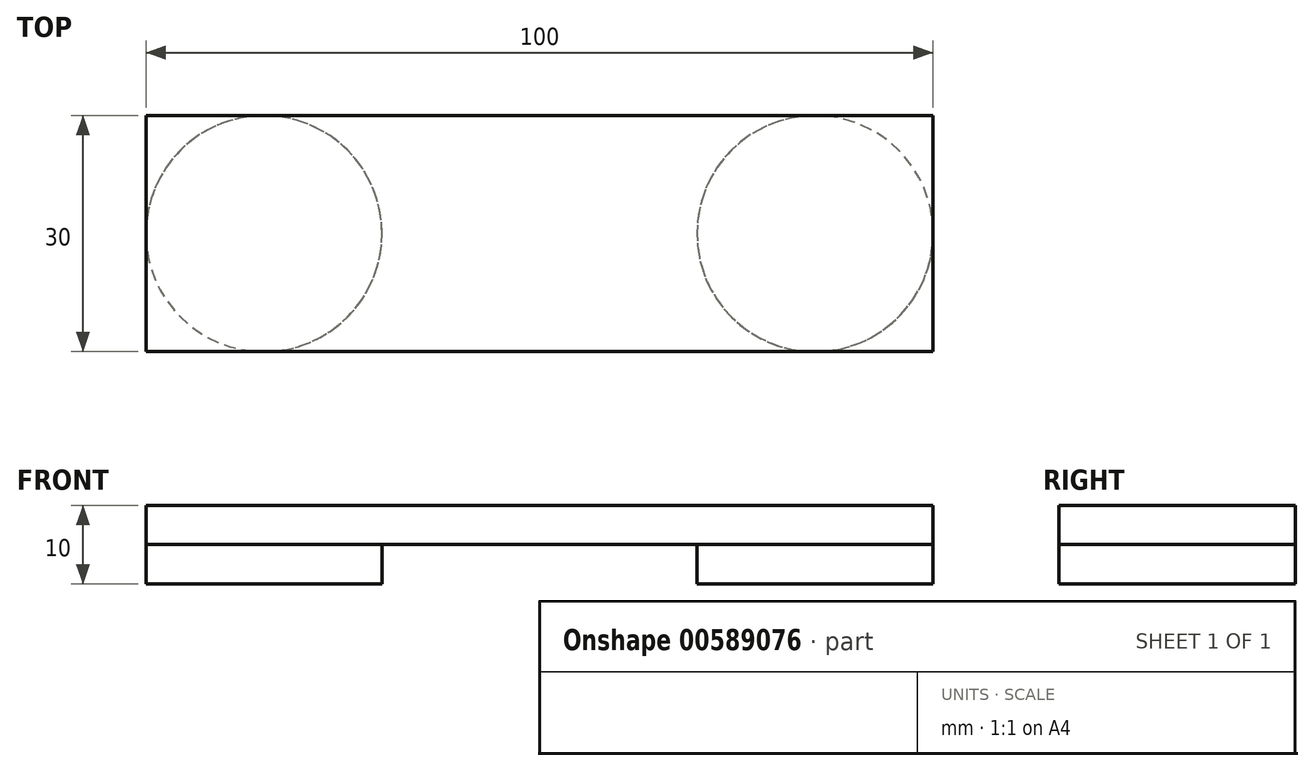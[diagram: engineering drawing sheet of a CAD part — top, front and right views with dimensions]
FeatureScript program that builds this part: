
annotation { "Feature Type Name" : "Feature", "Feature Type Description" : "" }
export const myFeature = defineFeature(function(context is Context, id is Id, definition is map)
    precondition{}
    {
        {
            var Q0;
            Q0=qCreatedBy(makeId("Top.planeOp"),FACE);
            var sketch = newSketch(context, id + "F0", { "sketchPlane" : qUnion([Q0])});
            skLineSegment(sketch, "E0.bottom", {"start": v(50, 15) * mm, "end": v(-50, 15) * mm});
            skLineSegment(sketch, "E0.top", {"start": v(50, -15) * mm, "end": v(-50, -15) * mm});
            skLineSegment(sketch, "E0.left", {"start": v(50, 15) * mm, "end": v(50, -15) * mm});
            skLineSegment(sketch, "E0.right", {"start": v(-50, 15) * mm, "end": v(-50, -15) * mm});
            skPoint(sketch, "E0.middle", {"position": v(0, 0) * mm});
            skSolve(sketch);
        }
        {
            var Q0;
            Q0=makeQuery(id+"F0.imprint","IMPRINT",FACE,{"disambiguationData":[TD([[makeQuery(id+"F0.imprint","IMPRINT",EDGE,{"derivedFrom":sQuery(id+"F0.wireOp",EDGE,"E0.bottom")}),1.0]])]});
            extrude(context, id + "F1", {"entities" : qUnion([Q0]), "depth" : 5 * mm, "offsetDistance" : 25 * mm});
        }
        {
            var Q0;
            Q0=makeQuery(id+"F1.opExtrude","CAP_FACE",FACE,{"disambiguationData":[OSD([sQuery(id+"F0.wireOp",EDGE,"E0.bottom"),sQuery(id+"F0.wireOp",EDGE,"E0.top"),sQuery(id+"F0.wireOp",EDGE,"E0.left"),sQuery(id+"F0.wireOp",EDGE,"E0.right")])],"isStart":false});
            var sketch = newSketch(context, id + "F2", { "sketchPlane" : qUnion([Q0])});
            skCircle(sketch, "E1", {"center": v(35, 0) * mm, "radius": 15 * mm});
            skCircle(sketch, "E2", {"center": v(-35, 0) * mm, "radius": 15 * mm});
            skSolve(sketch);
        }
        {
            var Q0;
            {var subQ0=sQuery(id+"F2.wireOp",EDGE,"E1");var subQ1=makeQuery(id+"F2.imprint","INTERSECT",VERTEX,{"derivedFrom":[makeQuery(id+"F1.opExtrude","CAP_EDGE",EDGE,{"disambiguationData":[OSD([sQuery(id+"F0.wireOp",EDGE,"E0.bottom")])],"isStart":false}),subQ0]});Q0=makeQuery(id+"F2.imprint","IMPRINT",FACE,{"disambiguationData":[TD([[makeQuery(id+"F2.imprint","IMPRINT",EDGE,{"disambiguationData":[TD([[subQ1,1.0]])],"derivedFrom":subQ0}),1.0]])]});}
            var Q1;
            {var subQ0=sQuery(id+"F2.wireOp",EDGE,"E2");var subQ1=makeQuery(id+"F2.imprint","INTERSECT",VERTEX,{"derivedFrom":[makeQuery(id+"F1.opExtrude","CAP_EDGE",EDGE,{"disambiguationData":[OSD([sQuery(id+"F0.wireOp",EDGE,"E0.right")])],"isStart":false}),subQ0]});Q1=makeQuery(id+"F2.imprint","IMPRINT",FACE,{"disambiguationData":[TD([[makeQuery(id+"F2.imprint","IMPRINT",EDGE,{"disambiguationData":[TD([[subQ1,1.0]])],"derivedFrom":subQ0}),1.0]])]});}
            extrude(context, id + "F3", {"entities" : qUnion([Q0, Q1]), "operationType" : NewBodyOperationType.ADD, "depth" : 5 * mm, "offsetDistance" : 25 * mm});
        }
        {
            var Q0;
            Q0=makeQuery(id+"F1.opExtrude","SWEPT_BODY",BODY,{"disambiguationData":[OSD([sQuery(id+"F0.wireOp",EDGE,"E0.bottom"),sQuery(id+"F0.wireOp",EDGE,"E0.top"),sQuery(id+"F0.wireOp",EDGE,"E0.left"),sQuery(id+"F0.wireOp",EDGE,"E0.right")])]});
            var Q1;
            {var subQ0=sQuery(id+"F0.wireOp",EDGE,"E0.bottom");Q1=makeQuery(id+"F3.boolean.opBoolean","SPLIT",EDGE,{"disambiguationData":[TD([makeQuery(id+"F1.opExtrude","SWEPT_FACE",FACE,{"disambiguationData":[OSD([subQ0])]}),makeQuery(id+"F1.opExtrude","CAP_FACE",FACE,{"disambiguationData":[OSD([subQ0,sQuery(id+"F0.wireOp",EDGE,"E0.top"),sQuery(id+"F0.wireOp",EDGE,"E0.left"),sQuery(id+"F0.wireOp",EDGE,"E0.right")])],"isStart":false}),makeQuery(id+"F3.opExtrude","SWEPT_FACE",FACE,{"disambiguationData":[OSD([sQuery(id+"F2.wireOp",EDGE,"E1")])]}),makeQuery(id+"F3.opExtrude","SWEPT_FACE",FACE,{"disambiguationData":[OSD([sQuery(id+"F2.wireOp",EDGE,"E2")])]})])],"derivedFrom":makeQuery(id+"F1.opExtrude","CAP_EDGE",EDGE,{"disambiguationData":[OSD([subQ0])],"isStart":false})});}
            transform(context, id + "F4", {"entities" : qUnion([Q0]), "transformType" : TransformType.ROTATION, "transformAxis" : qUnion([Q1]), "angle" : 180 * degree, "makeCopy" : false});
        }
    });
